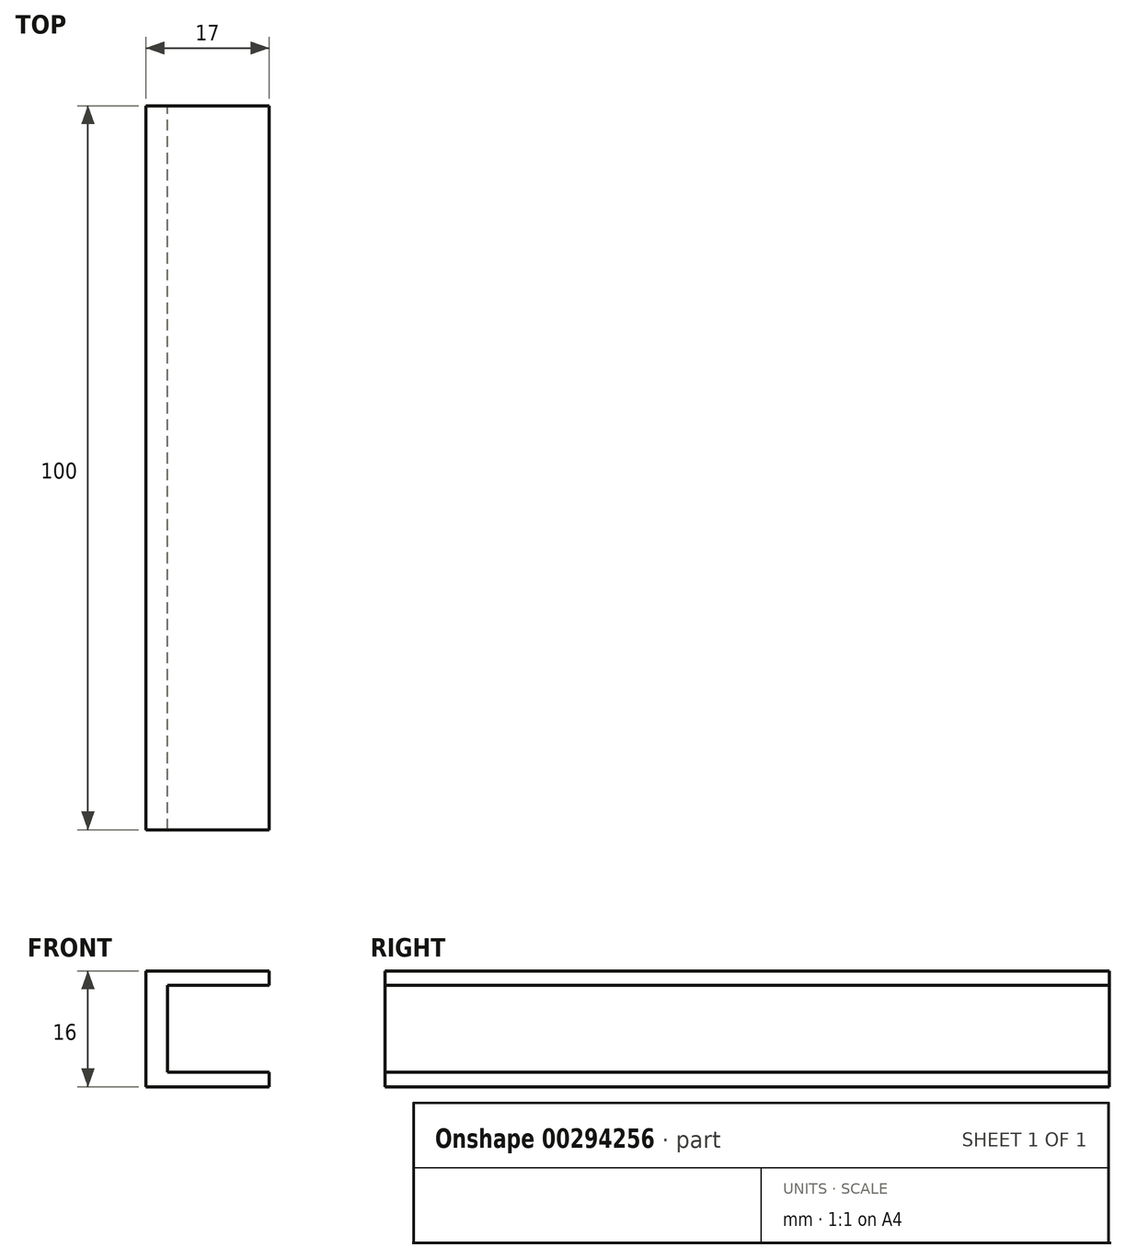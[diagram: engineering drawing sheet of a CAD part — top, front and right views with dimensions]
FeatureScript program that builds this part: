
annotation { "Feature Type Name" : "Feature", "Feature Type Description" : "" }
export const myFeature = defineFeature(function(context is Context, id is Id, definition is map)
    precondition{}
    {
        {
            var Q0;
            Q0=qCreatedBy(makeId("Front.planeOp"),FACE);
            var sketch = newSketch(context, id + "F0", { "sketchPlane" : qUnion([Q0])});
            skLineSegment(sketch, "E0", {"start": v(-17, 9.43) * mm, "end": v(-17, -6.57) * mm});
            skLineSegment(sketch, "E1", {"start": v(-17, -6.57) * mm, "end": v(0, -6.57) * mm});
            skLineSegment(sketch, "E2", {"start": v(-17, 9.43) * mm, "end": v(0, 9.43) * mm});
            skLineSegment(sketch, "E3", {"start": v(0, 9.43) * mm, "end": v(0, 7.43) * mm});
            skLineSegment(sketch, "E4", {"start": v(0, 7.43) * mm, "end": v(-14, 7.43) * mm});
            skLineSegment(sketch, "E5", {"start": v(-14, 7.43) * mm, "end": v(-14, -4.57) * mm});
            skLineSegment(sketch, "E6", {"start": v(-14, -4.57) * mm, "end": v(0, -4.57) * mm});
            skLineSegment(sketch, "E7", {"start": v(0, -4.57) * mm, "end": v(0, -6.57) * mm});
            skSolve(sketch);
        }
        {
            var Q0;
            Q0 = qSketchRegion(id + "F0", true);
            extrude(context, id + "F1", {"entities" : qUnion([Q0]), "depth" : 100 * mm});
        }
    });
